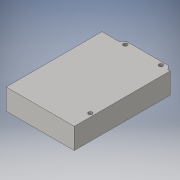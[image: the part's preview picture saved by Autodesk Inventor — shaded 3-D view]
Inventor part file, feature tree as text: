
AUTODESK INVENTOR PART (.ipt)
format: ipt  version: 2016 (Build 200138000, 138)  size: 119,296 bytes
history: native  units: in
note: dims shown in document units (in); Inventor stores cm internally (conversion verified against a paired STEP export)
features: extrude x2, sketch x2, chamfer x1
ambient origin geometry x8: Origin, YZ Plane, XZ Plane, XY Plane, X Axis, Y Axis, Z Axis, Center Point
bodies: Solid1 (feature_tree)
feature tree (5):
  extrude  "Extrusion1"  Depth=2.103in
  chamfer  "Chamfer1"  Distance=0.08in
  extrude  "Extrusion2"  Depth=0.116in
  sketch  "Sketch1"  dims[d0=2.958in d1=2.103in]
  sketch  "Sketch2"  dims[d2=1.473in d3=0.08in d4=0.116in d5=0.647in d6=0.0in d7=0.1in d8=0.125in d9=45.0deg d10=0.121in d11=0.1035in d12=0.121in d13=0.1035in d14=0.2965in d15=1.098in d16=0.599in d17=0.104in d18=0.121in d19=0.647in d20=0.0in d21=2.3715in d22=0.1925in]
